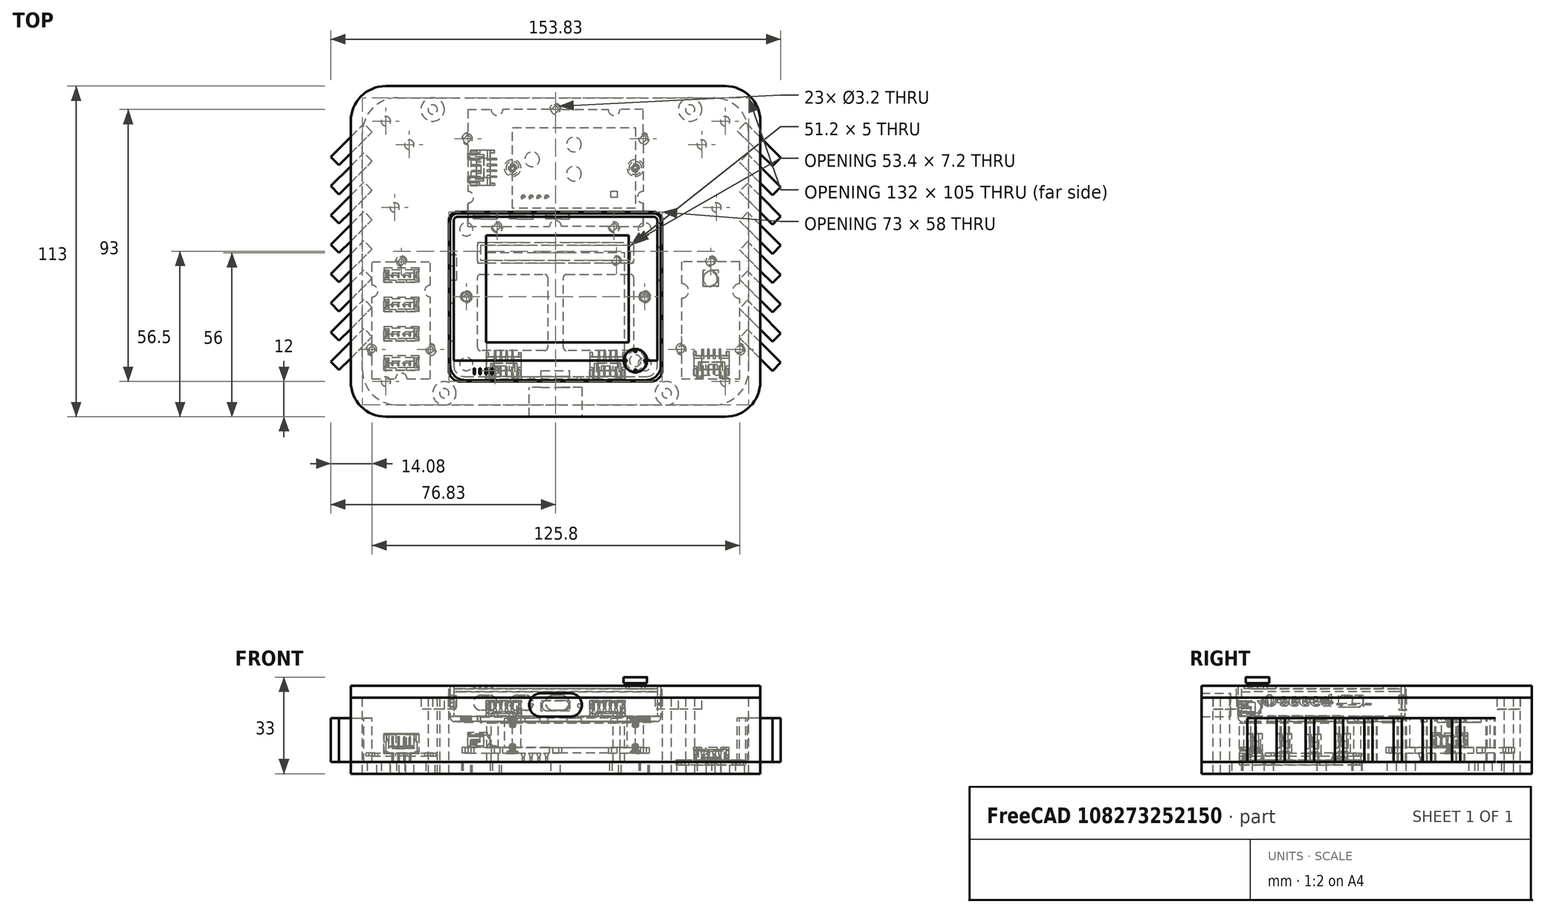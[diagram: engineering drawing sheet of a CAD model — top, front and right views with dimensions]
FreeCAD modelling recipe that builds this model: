
FCSTD DOCUMENT  (FreeCAD 0.20R29177 (Git))
Label: outBuildCopy2
License: All rights reserved
LicenseURL: http://en.wikipedia.org/wiki/All_rights_reserved
objects: Part::Cylinder×59, Part::Box×43, Part::Cut×32, Part::MultiFuse×21, Part::Feature×4, Sketcher::SketchObject×2
note: 161 computed .brp shape members not serialized (recipe doc carries the construction recipe); baked Part::Feature solids carry a one-line shape summary decoded from their .brp

FEATURE [Part::Feature] Feature  label="Grove I2C hub"
  Placement = pos=(15,60,9) rot=(0,0,1;3.14159rad)
  shape: bbox 24 x 42 x 9.849 mm, 365 faces, 5 solids (baked)
FEATURE [Part::Feature] Feature001  label="Grove_BME280"
  Placement = pos=(113,14,3) rot=(0.57735,0.57735,0.57735;2.0944rad)
  shape: bbox 23.8 x 41.9 x 6.016 mm, 221 faces, 2 solids (baked)
FEATURE [Part::Box] Box043  label="ips7100"
  AttacherType = Attacher::AttachEngine3D
  Height = 13.4
  Length = 47.1
  Width = 43.1
FEATURE [Part::Cylinder] Cylinder045  label="Cylinder"
  Angle = 360
  AttacherType = Attacher::AttachEngine3D
  FirstAngle = 0
  Height = 20
  Placement = pos=(2.75,2.75,0) rot=(0,0,1;0rad)
  Radius = 1.2
  SecondAngle = 0
FEATURE [Part::Cylinder] Cylinder046
  Angle = 360
  AttacherType = Attacher::AttachEngine3D
  FirstAngle = 0
  Height = 20
  Placement = pos=(44.35,40.35,0) rot=(0,0,1;0rad)
  Radius = 1.2
  SecondAngle = 0
FEATURE [Part::MultiFuse] Fusion030
  Shapes = -> [Cylinder045,Cylinder046]
FEATURE [Part::Cut] Cut012  label="ips7100s"
  Base = -> Box043
  Placement = pos=(46.5,13,4) rot=(0,0,1;0rad)
  Tool = -> Fusion030
FEATURE [Part::Feature] Feature002  label="Wio Terminal"
  Placement = pos=(70,41,30) rot=(0,0,1;0rad)
  shape: bbox 73.03 x 57.91 x 15.61 mm, 2405 faces, 30 solids (baked)
FEATURE [Part::Feature] Feature003  label="Seed Grove SCD30"
  Placement = pos=(40,65,9) rot=(1,0,0;4.71239rad)
  shape: bbox 64 x 44 x 15.1 mm, 422 faces, 13 solids (baked)
FEATURE [Part::Box] Box  label="base"
  AttacherType = Attacher::AttachEngine3D
  Height = 4
  Length = 140
  Width = 113
FEATURE [Part::Cylinder] Cylinder047  label="Cylinder048"
  Angle = 360
  AttacherType = Attacher::AttachEngine3D
  FirstAngle = 0
  Height = 10
  Placement = pos=(7.25,23,0) rot=(0,0,1;0rad)
  Radius = 1.6
  SecondAngle = 0
FEATURE [Part::Cylinder] Cylinder048  label="Cylinder049"
  Angle = 360
  AttacherType = Attacher::AttachEngine3D
  FirstAngle = 0
  Height = 10
  Placement = pos=(27.25,23,0) rot=(0,0,1;0rad)
  Radius = 1.6
  SecondAngle = 0
FEATURE [Part::Cylinder] Cylinder049  label="Cylinder050"
  Angle = 360
  AttacherType = Attacher::AttachEngine3D
  FirstAngle = 0
  Height = 10
  Placement = pos=(17.25,53,0) rot=(0,0,1;0rad)
  Radius = 1.6
  SecondAngle = 0
FEATURE [Part::MultiFuse] Fusion  label="i2cCuts"
  Shapes = -> [Cylinder047,Cylinder048,Cylinder049]
FEATURE [Part::Cylinder] Cylinder050  label="Cylinder051"
  Angle = 360
  AttacherType = Attacher::AttachEngine3D
  FirstAngle = 0
  Height = 10
  Placement = pos=(7.25,23,0) rot=(0,0,1;0rad)
  Radius = 1.6
  SecondAngle = 0
FEATURE [Part::Cylinder] Cylinder051  label="Cylinder052"
  Angle = 360
  AttacherType = Attacher::AttachEngine3D
  FirstAngle = 0
  Height = 10
  Placement = pos=(27.25,23,0) rot=(0,0,1;0rad)
  Radius = 1.6
  SecondAngle = 0
FEATURE [Part::Cylinder] Cylinder052  label="Cylinder053"
  Angle = 360
  AttacherType = Attacher::AttachEngine3D
  FirstAngle = 0
  Height = 10
  Placement = pos=(17.25,53,0) rot=(0,0,1;0rad)
  Radius = 1.6
  SecondAngle = 0
FEATURE [Part::MultiFuse] Fusion031  label="scdCuts001"
  Placement = pos=(105.8,0,0) rot=(0,0,1;0rad)
  Shapes = -> [Cylinder050,Cylinder051,Cylinder052]
FEATURE [Part::Cylinder] Cylinder053  label="Cylinder054"
  Angle = 360
  AttacherType = Attacher::AttachEngine3D
  FirstAngle = 0
  Height = 20
  Placement = pos=(2.75,2.75,0) rot=(0,0,1;0rad)
  Radius = 1.6
  SecondAngle = 0
FEATURE [Part::Cylinder] Cylinder054  label="Cylinder055"
  Angle = 360
  AttacherType = Attacher::AttachEngine3D
  FirstAngle = 0
  Height = 20
  Placement = pos=(44.35,40.35,0) rot=(0,0,1;0rad)
  Radius = 1.6
  SecondAngle = 0
FEATURE [Part::MultiFuse] Fusion032  label="ipsCuts"
  Placement = pos=(46.5,13,0) rot=(0,0,1;0rad)
  Shapes = -> [Cylinder053,Cylinder054]
FEATURE [Part::Cylinder] Cylinder055  label="Cylinder056"
  Angle = 360
  AttacherType = Attacher::AttachEngine3D
  FirstAngle = 0
  Height = 10
  Placement = pos=(50,65,0) rot=(0,0,1;0rad)
  Radius = 1.6
  SecondAngle = 0
FEATURE [Part::Cylinder] Cylinder056  label="Cylinder057"
  Angle = 360
  AttacherType = Attacher::AttachEngine3D
  FirstAngle = 0
  Height = 10
  Placement = pos=(90,65,0) rot=(0,0,1;0rad)
  Radius = 1.6
  SecondAngle = 0
FEATURE [Part::Cylinder] Cylinder057  label="Cylinder058"
  Angle = 360
  AttacherType = Attacher::AttachEngine3D
  FirstAngle = 0
  Height = 10
  Placement = pos=(100,95,0) rot=(0,0,1;0rad)
  Radius = 1.6
  SecondAngle = 0
FEATURE [Part::Cylinder] Cylinder058  label="Cylinder059"
  Angle = 360
  AttacherType = Attacher::AttachEngine3D
  FirstAngle = 0
  Height = 10
  Placement = pos=(40,95,0) rot=(0,0,1;0rad)
  Radius = 1.6
  SecondAngle = 0
FEATURE [Part::Cylinder] Cylinder059  label="Cylinder060"
  Angle = 360
  AttacherType = Attacher::AttachEngine3D
  FirstAngle = 0
  Height = 10
  Placement = pos=(70,105,0) rot=(0,0,1;0rad)
  Radius = 1.6
  SecondAngle = 0
FEATURE [Part::MultiFuse] Fusion033  label="scdCuts"
  Shapes = -> [Cylinder055,Cylinder056,Cylinder057,Cylinder058,Cylinder059]
FEATURE [Part::Cylinder] Cylinder060  label="Cylinder061"
  Angle = 360
  AttacherType = Attacher::AttachEngine3D
  FirstAngle = 0
  Height = 20
  Placement = pos=(39.5,41,0) rot=(0,0,1;0rad)
  Radius = 1.6
  SecondAngle = 0
FEATURE [Part::Cylinder] Cylinder061  label="Cylinder062"
  Angle = 360
  AttacherType = Attacher::AttachEngine3D
  FirstAngle = 0
  Height = 20
  Placement = pos=(100.5,41,0) rot=(0,0,1;0rad)
  Radius = 1.6
  SecondAngle = 0
FEATURE [Part::MultiFuse] Fusion034  label="wioCuts"
  Shapes = -> [Cylinder060,Cylinder061]
FEATURE [Part::MultiFuse] Fusion035  label="cuts"
  Shapes = -> [Fusion,Fusion031,Fusion032,Fusion033,Fusion034]
FEATURE [Part::Cut] Cut  label="base001"
  Base = -> Box
  Tool = -> Fusion035
FEATURE [Part::Cylinder] Cylinder062  label="Cylinder063"
  Angle = 360
  AttacherType = Attacher::AttachEngine3D
  FirstAngle = 0
  Height = 10
  Placement = pos=(12,12,0) rot=(0,0,1;0rad)
  Radius = 1.6
  SecondAngle = 0
FEATURE [Part::Cylinder] Cylinder063  label="Cylinder064"
  Angle = 360
  AttacherType = Attacher::AttachEngine3D
  FirstAngle = 0
  Height = 10
  Placement = pos=(128,12,0) rot=(0,0,1;0rad)
  Radius = 1.6
  SecondAngle = 0
FEATURE [Part::Cylinder] Cylinder064  label="Cylinder065"
  Angle = 360
  AttacherType = Attacher::AttachEngine3D
  FirstAngle = 0
  Height = 10
  Placement = pos=(12,101,0) rot=(0,0,1;0rad)
  Radius = 1.6
  SecondAngle = 0
FEATURE [Part::Cylinder] Cylinder065  label="Cylinder066"
  Angle = 360
  AttacherType = Attacher::AttachEngine3D
  FirstAngle = 0
  Height = 10
  Placement = pos=(128,101,0) rot=(0,0,1;0rad)
  Radius = 1.6
  SecondAngle = 0
FEATURE [Part::MultiFuse] Fusion036  label="outerCuts"
  Shapes = -> [Cylinder062,Cylinder063,Cylinder064,Cylinder065]
FEATURE [Part::Cut] Cut013  label="base003"
  Base = -> Cut
  Tool = -> Fusion036
FEATURE [Part::Box] Box044  label="base002"
  AttacherType = Attacher::AttachEngine3D
  Height = 4
  Length = 12
  Width = 12
FEATURE [Part::Cylinder] Cylinder  label="Cylinder067"
  Angle = 360
  AttacherType = Attacher::AttachEngine3D
  FirstAngle = 0
  Height = 10
  Placement = pos=(12,12,0) rot=(0,-0.707107,0.707107;0rad)
  Radius = 12
  SecondAngle = 0
FEATURE [Part::Cut] Cut014  label="cutOut"
  Base = -> Box044
  Tool = -> Cylinder
FEATURE [Part::Box] Box045  label="base004"
  AttacherType = Attacher::AttachEngine3D
  Height = 4
  Length = 12
  Width = 12
FEATURE [Part::Cylinder] Cylinder066  label="Cylinder068"
  Angle = 360
  AttacherType = Attacher::AttachEngine3D
  FirstAngle = 0
  Height = 10
  Placement = pos=(12,12,0) rot=(0,-0.707107,0.707107;0rad)
  Radius = 12
  SecondAngle = 0
FEATURE [Part::Cut] Cut015  label="cutOut001"
  Base = -> Box045
  Placement = pos=(140,-5.2e-15,0) rot=(0,0,1;1.5708rad)
  Tool = -> Cylinder066
FEATURE [Part::Box] Box046  label="base005"
  AttacherType = Attacher::AttachEngine3D
  Height = 4
  Length = 12
  Width = 12
FEATURE [Part::Cylinder] Cylinder067  label="Cylinder069"
  Angle = 360
  AttacherType = Attacher::AttachEngine3D
  FirstAngle = 0
  Height = 10
  Placement = pos=(12,12,0) rot=(0,-0.707107,0.707107;0rad)
  Radius = 12
  SecondAngle = 0
FEATURE [Part::Cut] Cut016  label="cutOut002"
  Base = -> Box046
  Placement = pos=(140,113,0) rot=(0,0,1;3.14159rad)
  Tool = -> Cylinder067
FEATURE [Part::Box] Box047  label="base006"
  AttacherType = Attacher::AttachEngine3D
  Height = 4
  Length = 12
  Width = 12
FEATURE [Part::Cylinder] Cylinder068  label="Cylinder070"
  Angle = 360
  AttacherType = Attacher::AttachEngine3D
  FirstAngle = 0
  Height = 10
  Placement = pos=(12,12,0) rot=(0,-0.707107,0.707107;0rad)
  Radius = 12
  SecondAngle = 0
FEATURE [Part::Cut] Cut017  label="cutOut003"
  Base = -> Box047
  Placement = pos=(0,113,0) rot=(0,0,1;4.71239rad)
  Tool = -> Cylinder068
FEATURE [Part::MultiFuse] Fusion037  label="cutOut004"
  Shapes = -> [Cut014,Cut015,Cut016,Cut017]
FEATURE [Part::Cut] Cut018
  Base = -> Cut013
  Tool = -> Fusion037
FEATURE [Part::Cylinder] Cylinder069  label="Cylinder071"
  Angle = 360
  AttacherType = Attacher::AttachEngine3D
  FirstAngle = 0
  Height = 10
  Placement = pos=(15,71.5,0) rot=(0,0,1;0rad)
  Radius = 1.6
  SecondAngle = 0
FEATURE [Part::Cylinder] Cylinder070  label="Cylinder072"
  Angle = 360
  AttacherType = Attacher::AttachEngine3D
  FirstAngle = 0
  Height = 10
  Placement = pos=(125,71.5,0) rot=(0,0,1;0rad)
  Radius = 1.6
  SecondAngle = 0
FEATURE [Part::MultiFuse] Fusion038  label="cuts001"
  Shapes = -> [Cylinder069,Cylinder070]
FEATURE [Part::Cut] Cut019  label="base007"
  Base = -> Cut018
  Tool = -> Fusion038
FEATURE [Part::Cylinder] Cylinder071  label="Cylinder073"
  Angle = 360
  AttacherType = Attacher::AttachEngine3D
  FirstAngle = 0
  Height = 10
  Placement = pos=(20,93,0) rot=(0,0,1;0rad)
  Radius = 1.6
  SecondAngle = 0
FEATURE [Part::Cylinder] Cylinder072  label="Cylinder074"
  Angle = 360
  AttacherType = Attacher::AttachEngine3D
  FirstAngle = 0
  Height = 10
  Placement = pos=(120,93,0) rot=(0,0,1;0rad)
  Radius = 1.6
  SecondAngle = 0
FEATURE [Part::MultiFuse] Fusion039  label="wallMounts"
  Shapes = -> [Cylinder071,Cylinder072]
FEATURE [Part::Cut] Cut020  label="base008"
  Base = -> Cut019
  Tool = -> Fusion039
FEATURE [Part::Box] Box048  label="top"
  AttacherType = Attacher::AttachEngine3D
  Height = 4
  Length = 140
  Width = 113
FEATURE [Part::Box] Box049  label="base009"
  AttacherType = Attacher::AttachEngine3D
  Height = 4
  Length = 12
  Width = 12
FEATURE [Part::Box] Box050  label="base010"
  AttacherType = Attacher::AttachEngine3D
  Height = 4
  Length = 12
  Width = 12
FEATURE [Part::Box] Box051  label="base011"
  AttacherType = Attacher::AttachEngine3D
  Height = 4
  Length = 12
  Width = 12
FEATURE [Part::Box] Box052  label="base012"
  AttacherType = Attacher::AttachEngine3D
  Height = 4
  Length = 12
  Width = 12
FEATURE [Part::Cylinder] Cylinder073  label="Cylinder075"
  Angle = 360
  AttacherType = Attacher::AttachEngine3D
  FirstAngle = 0
  Height = 10
  Placement = pos=(12,12,0) rot=(0,-0.707107,0.707107;0rad)
  Radius = 12
  SecondAngle = 0
FEATURE [Part::Cut] Cut021  label="cutOut005"
  Base = -> Box049
  Tool = -> Cylinder073
FEATURE [Part::Cylinder] Cylinder074  label="Cylinder076"
  Angle = 360
  AttacherType = Attacher::AttachEngine3D
  FirstAngle = 0
  Height = 10
  Placement = pos=(12,12,0) rot=(0,-0.707107,0.707107;0rad)
  Radius = 12
  SecondAngle = 0
FEATURE [Part::Cut] Cut022  label="cutOut006"
  Base = -> Box050
  Placement = pos=(140,-5.2e-15,0) rot=(0,0,1;1.5708rad)
  Tool = -> Cylinder074
FEATURE [Part::Cylinder] Cylinder075  label="Cylinder077"
  Angle = 360
  AttacherType = Attacher::AttachEngine3D
  FirstAngle = 0
  Height = 10
  Placement = pos=(12,12,0) rot=(0,-0.707107,0.707107;0rad)
  Radius = 12
  SecondAngle = 0
FEATURE [Part::Cut] Cut023  label="cutOut007"
  Base = -> Box051
  Placement = pos=(140,113,0) rot=(0,0,1;3.14159rad)
  Tool = -> Cylinder075
FEATURE [Part::Cylinder] Cylinder076  label="Cylinder078"
  Angle = 360
  AttacherType = Attacher::AttachEngine3D
  FirstAngle = 0
  Height = 10
  Placement = pos=(12,12,0) rot=(0,-0.707107,0.707107;0rad)
  Radius = 12
  SecondAngle = 0
FEATURE [Part::Cut] Cut024  label="cutOut008"
  Base = -> Box052
  Placement = pos=(0,113,0) rot=(0,0,-1;1.5708rad)
  Tool = -> Cylinder076
FEATURE [Part::MultiFuse] Fusion040  label="cutOut009"
  Shapes = -> [Cut021,Cut022,Cut023,Cut024]
FEATURE [Part::Cut] Cut025  label="top001"
  Base = -> Box048
  Placement = pos=(0,0,26) rot=(0,0,1;0rad)
  Tool = -> Fusion040
FEATURE [Part::Box] Box053  label="Cube"
  AttacherType = Attacher::AttachEngine3D
  Height = 10
  Length = 73
  Placement = pos=(33.5,12,26) rot=(0,0,1;0rad)
  Width = 58
FEATURE [Part::Box] Box054  label="Cube001"
  AttacherType = Attacher::AttachEngine3D
  Height = 10
  Length = 3
  Placement = pos=(33.5,67,26) rot=(0,0,1;0rad)
  Width = 3
FEATURE [Part::Cylinder] Cylinder077  label="Cylinder079"
  Angle = 360
  AttacherType = Attacher::AttachEngine3D
  FirstAngle = 0
  Height = 10
  Placement = pos=(36.5,67,26) rot=(0,0,1;0rad)
  Radius = 3
  SecondAngle = 0
FEATURE [Part::Cut] Cut026  label="outCutsDisplay"
  Base = -> Box054
  Tool = -> Cylinder077
FEATURE [Part::Box] Box055  label="Cube002"
  AttacherType = Attacher::AttachEngine3D
  Height = 10
  Length = 3
  Placement = pos=(33.5,67,26) rot=(0,0,1;0rad)
  Width = 3
FEATURE [Part::Cylinder] Cylinder078  label="Cylinder080"
  Angle = 360
  AttacherType = Attacher::AttachEngine3D
  FirstAngle = 0
  Height = 10
  Placement = pos=(36.5,67,26) rot=(0,0,1;0rad)
  Radius = 3
  SecondAngle = 0
FEATURE [Part::Cut] Cut027  label="outCutsDisplay001"
  Base = -> Box055
  Placement = pos=(36.5,103.5,0) rot=(0,0,1;4.71239rad)
  Tool = -> Cylinder078
FEATURE [Part::Box] Box057  label="Cube004"
  AttacherType = Attacher::AttachEngine3D
  Height = 10
  Length = 4
  Placement = pos=(32.5,67,26) rot=(0,0,1;0rad)
  Width = 4
FEATURE [Part::Cylinder] Cylinder080  label="Cylinder082"
  Angle = 360
  AttacherType = Attacher::AttachEngine3D
  FirstAngle = 0
  Height = 10
  Placement = pos=(36.5,67,26) rot=(0,0,1;0rad)
  Radius = 4
  SecondAngle = 0
FEATURE [Part::Cut] Cut029  label="outCutsDisplay003"
  Base = -> Box057
  Placement = pos=(104.5,-20.5,0) rot=(0,0,1;1.5708rad)
  Tool = -> Cylinder080
FEATURE [Part::Box] Box058  label="Cube005"
  AttacherType = Attacher::AttachEngine3D
  Height = 10
  Length = 4
  Placement = pos=(32.5,67,26) rot=(0,0,1;0rad)
  Width = 4
FEATURE [Part::Cylinder] Cylinder081  label="Cylinder083"
  Angle = 360
  AttacherType = Attacher::AttachEngine3D
  FirstAngle = 0
  Height = 10
  Placement = pos=(36.5,67,26) rot=(0,0,1;0rad)
  Radius = 4
  SecondAngle = 0
FEATURE [Part::Cut] Cut030  label="outCutsDisplay004"
  Base = -> Box058
  Placement = pos=(139,83,0) rot=(0,0,1;3.14159rad)
  Tool = -> Cylinder081
FEATURE [Part::MultiFuse] Fusion041  label="displayCuts"
  Shapes = -> [Cut029,Cut030,Cut026,Cut027]
FEATURE [Part::Cut] Cut031  label="topCut"
  Base = -> Box053
  Tool = -> Fusion041
FEATURE [Part::Cut] Cut032  label="top002"
  Base = -> Cut025
  Tool = -> Cut031
FEATURE [Part::Box] Box059  label="base013"
  AttacherType = Attacher::AttachEngine3D
  Height = 26
  Length = 140
  Width = 113
FEATURE [Part::Box] Box060  label="base014"
  AttacherType = Attacher::AttachEngine3D
  Height = 26
  Length = 12
  Width = 12
FEATURE [Part::Box] Box061  label="base015"
  AttacherType = Attacher::AttachEngine3D
  Height = 26
  Length = 12
  Width = 12
FEATURE [Part::Box] Box062  label="base016"
  AttacherType = Attacher::AttachEngine3D
  Height = 26
  Length = 12
  Width = 12
FEATURE [Part::Box] Box063  label="base017"
  AttacherType = Attacher::AttachEngine3D
  Height = 26
  Length = 12
  Width = 12
FEATURE [Part::Cylinder] Cylinder082  label="Cylinder084"
  Angle = 360
  AttacherType = Attacher::AttachEngine3D
  FirstAngle = 0
  Height = 26
  Placement = pos=(12,12,0) rot=(0,-0.707107,0.707107;0rad)
  Radius = 12
  SecondAngle = 0
FEATURE [Part::Cut] Cut033  label="cutOut010"
  Base = -> Box060
  Tool = -> Cylinder082
FEATURE [Part::Cylinder] Cylinder083  label="Cylinder085"
  Angle = 360
  AttacherType = Attacher::AttachEngine3D
  FirstAngle = 0
  Height = 26
  Placement = pos=(12,12,0) rot=(0,-0.707107,0.707107;0rad)
  Radius = 12
  SecondAngle = 0
FEATURE [Part::Cut] Cut034  label="cutOut011"
  Base = -> Box061
  Placement = pos=(140,-5.2e-15,0) rot=(0,0,1;1.5708rad)
  Tool = -> Cylinder083
FEATURE [Part::Cylinder] Cylinder084  label="Cylinder086"
  Angle = 360
  AttacherType = Attacher::AttachEngine3D
  FirstAngle = 0
  Height = 26
  Placement = pos=(12,12,0) rot=(0,-0.707107,0.707107;0rad)
  Radius = 12
  SecondAngle = 0
FEATURE [Part::Cut] Cut035  label="cutOut012"
  Base = -> Box062
  Placement = pos=(140,113,0) rot=(0,0,1;3.14159rad)
  Tool = -> Cylinder084
FEATURE [Part::Cylinder] Cylinder085  label="Cylinder087"
  Angle = 360
  AttacherType = Attacher::AttachEngine3D
  FirstAngle = 0
  Height = 26
  Placement = pos=(12,12,0) rot=(0,-0.707107,0.707107;0rad)
  Radius = 12
  SecondAngle = 0
FEATURE [Part::Cut] Cut036  label="cutOut013"
  Base = -> Box063
  Placement = pos=(0,113,0) rot=(0,0,-1;1.5708rad)
  Tool = -> Cylinder085
FEATURE [Part::MultiFuse] Fusion042  label="cuts002"
  Shapes = -> [Cut036,Cut033,Cut034,Cut035]
FEATURE [Part::Cut] Cut037  label="wall"
  Base = -> Box059
  Tool = -> Fusion042
FEATURE [Part::Box] Box064  label="base018"
  AttacherType = Attacher::AttachEngine3D
  Height = 26
  Length = 132
  Placement = pos=(4,4,0) rot=(0,0,1;0rad)
  Width = 105
FEATURE [Part::Box] Box065  label="base019"
  AttacherType = Attacher::AttachEngine3D
  Height = 26
  Length = 12
  Width = 12
FEATURE [Part::Box] Box066  label="base020"
  AttacherType = Attacher::AttachEngine3D
  Height = 26
  Length = 12
  Width = 12
FEATURE [Part::Box] Box067  label="base021"
  AttacherType = Attacher::AttachEngine3D
  Height = 26
  Length = 12
  Width = 12
FEATURE [Part::Box] Box068  label="base022"
  AttacherType = Attacher::AttachEngine3D
  Height = 26
  Length = 12
  Width = 12
FEATURE [Part::Cylinder] Cylinder086  label="Cylinder088"
  Angle = 360
  AttacherType = Attacher::AttachEngine3D
  FirstAngle = 0
  Height = 26
  Placement = pos=(12,12,0) rot=(0,-0.707107,0.707107;0rad)
  Radius = 12
  SecondAngle = 0
FEATURE [Part::Cut] Cut038  label="cutOut014"
  Base = -> Box065
  Placement = pos=(4,4,0) rot=(0,0,1;0rad)
  Tool = -> Cylinder086
FEATURE [Part::Cylinder] Cylinder087  label="Cylinder089"
  Angle = 360
  AttacherType = Attacher::AttachEngine3D
  FirstAngle = 0
  Height = 26
  Placement = pos=(12,12,0) rot=(0,-0.707107,0.707107;0rad)
  Radius = 12
  SecondAngle = 0
FEATURE [Part::Cut] Cut039  label="cutOut015"
  Base = -> Box066
  Placement = pos=(136,4,0) rot=(0,0,1;1.5708rad)
  Tool = -> Cylinder087
FEATURE [Part::Cylinder] Cylinder088  label="Cylinder090"
  Angle = 360
  AttacherType = Attacher::AttachEngine3D
  FirstAngle = 0
  Height = 26
  Placement = pos=(12,12,0) rot=(0,-0.707107,0.707107;0rad)
  Radius = 12
  SecondAngle = 0
FEATURE [Part::Cut] Cut040  label="cutOut016"
  Base = -> Box067
  Placement = pos=(136,109,0) rot=(0,0,1;3.14159rad)
  Tool = -> Cylinder088
FEATURE [Part::Cylinder] Cylinder089  label="Cylinder091"
  Angle = 360
  AttacherType = Attacher::AttachEngine3D
  FirstAngle = 0
  Height = 26
  Placement = pos=(12,12,0) rot=(0,-0.707107,0.707107;0rad)
  Radius = 12
  SecondAngle = 0
FEATURE [Part::Cut] Cut041  label="cutOut017"
  Base = -> Box068
  Placement = pos=(4,109,0) rot=(0,0,-1;1.5708rad)
  Tool = -> Cylinder089
FEATURE [Part::MultiFuse] Fusion043  label="cuts003"
  Shapes = -> [Cut041,Cut038,Cut039,Cut040]
FEATURE [Part::Cut] Cut042  label="wallCut"
  Base = -> Box064
  Tool = -> Fusion043
FEATURE [Part::Cut] Cut043  label="wall001"
  Base = -> Cut037
  Tool = -> Cut042
FEATURE [Part::Cylinder] Cylinder091  label="Cylinder093"
  Angle = 360
  AttacherType = Attacher::AttachEngine3D
  FirstAngle = 0
  Height = 4
  Placement = pos=(108,8,0) rot=(0,0,1;0rad)
  Radius = 4
  SecondAngle = 0
FEATURE [Part::Cylinder] Cylinder092  label="Cylinder094"
  Angle = 360
  AttacherType = Attacher::AttachEngine3D
  FirstAngle = 0
  Height = 4
  Placement = pos=(32,8,0) rot=(0,0,1;0rad)
  Radius = 4
  SecondAngle = 0
FEATURE [Part::Cylinder] Cylinder093  label="Cylinder095"
  Angle = 360
  AttacherType = Attacher::AttachEngine3D
  FirstAngle = 0
  Height = 4
  Placement = pos=(116,105,0) rot=(0,0,1;0rad)
  Radius = 4
  SecondAngle = 0
FEATURE [Part::Cylinder] Cylinder094  label="Cylinder096"
  Angle = 360
  AttacherType = Attacher::AttachEngine3D
  FirstAngle = 0
  Height = 4
  Placement = pos=(28,105,0) rot=(0,0,1;0rad)
  Radius = 4
  SecondAngle = 0
FEATURE [Part::MultiFuse] Fusion044  label="topMountIns"
  Placement = pos=(0,0,22) rot=(0,0,1;0rad)
  Shapes = -> [Cylinder091,Cylinder092,Cylinder093,Cylinder094]
FEATURE [Part::Cylinder] Cylinder095  label="Cylinder097"
  Angle = 360
  AttacherType = Attacher::AttachEngine3D
  FirstAngle = 0
  Height = 26
  Placement = pos=(108,8,0) rot=(0,0,1;0rad)
  Radius = 1.6
  SecondAngle = 0
FEATURE [Part::Cylinder] Cylinder096  label="Cylinder098"
  Angle = 360
  AttacherType = Attacher::AttachEngine3D
  FirstAngle = 0
  Height = 26
  Placement = pos=(32,8,0) rot=(0,0,1;0rad)
  Radius = 1.6
  SecondAngle = 0
FEATURE [Part::Cylinder] Cylinder097  label="Cylinder099"
  Angle = 360
  AttacherType = Attacher::AttachEngine3D
  FirstAngle = 0
  Height = 26
  Placement = pos=(116,105,0) rot=(0,0,1;0rad)
  Radius = 1.6
  SecondAngle = 0
FEATURE [Part::Cylinder] Cylinder098  label="Cylinder100"
  Angle = 360
  AttacherType = Attacher::AttachEngine3D
  FirstAngle = 0
  Height = 26
  Placement = pos=(28,105,0) rot=(0,0,1;0rad)
  Radius = 1.6
  SecondAngle = 0
FEATURE [Part::MultiFuse] Fusion045  label="bottomCuts"
  Shapes = -> [Cylinder095,Cylinder096,Cylinder097,Cylinder098]
FEATURE [Part::Cylinder] Cylinder099  label="Cylinder101"
  Angle = 360
  AttacherType = Attacher::AttachEngine3D
  FirstAngle = 0
  Height = 26
  Placement = pos=(108,8,0) rot=(0,0,1;0rad)
  Radius = 1.6
  SecondAngle = 0
FEATURE [Part::Cylinder] Cylinder100  label="Cylinder102"
  Angle = 360
  AttacherType = Attacher::AttachEngine3D
  FirstAngle = 0
  Height = 26
  Placement = pos=(32,8,0) rot=(0,0,1;0rad)
  Radius = 1.6
  SecondAngle = 0
FEATURE [Part::Cylinder] Cylinder101  label="Cylinder103"
  Angle = 360
  AttacherType = Attacher::AttachEngine3D
  FirstAngle = 0
  Height = 26
  Placement = pos=(116,105,0) rot=(0,0,1;0rad)
  Radius = 1.6
  SecondAngle = 0
FEATURE [Part::Cylinder] Cylinder102  label="Cylinder104"
  Angle = 360
  AttacherType = Attacher::AttachEngine3D
  FirstAngle = 0
  Height = 26
  Placement = pos=(28,105,0) rot=(0,0,1;0rad)
  Radius = 1.6
  SecondAngle = 0
FEATURE [Part::MultiFuse] Fusion046  label="topMountTop"
  Shapes = -> [Cylinder099,Cylinder100,Cylinder101,Cylinder102]
FEATURE [Part::Box] Box069  label="usbCCut"
  AttacherType = Attacher::AttachEngine3D
  Height = 8
  Length = 10
  Placement = pos=(65,0,19.5) rot=(0,0,1;0rad)
  Width = 10
FEATURE [Part::Cylinder] Cylinder103  label="usbCCut001"
  Angle = 360
  AttacherType = Attacher::AttachEngine3D
  FirstAngle = 0
  Height = 10
  Placement = pos=(65,10,23.5) rot=(1,0,0;1.5708rad)
  Radius = 4
  SecondAngle = 0
FEATURE [Part::Cylinder] Cylinder104  label="usbCCut002"
  Angle = 360
  AttacherType = Attacher::AttachEngine3D
  FirstAngle = 0
  Height = 10
  Placement = pos=(75,10,23.5) rot=(1,0,0;1.5708rad)
  Radius = 4
  SecondAngle = 0
FEATURE [Part::MultiFuse] Fusion047  label="usbCCut003"
  Shapes = -> [Box069,Cylinder103,Cylinder104]
FEATURE [Part::Box] Box070  label="ventCut"
  AttacherType = Attacher::AttachEngine3D
  Height = 15
  Length = 16
  Placement = pos=(-4,16,0) rot=(0,0,1;0.785398rad)
  Width = 4
FEATURE [Part::Box] Box071  label="ventCut001"
  AttacherType = Attacher::AttachEngine3D
  Height = 15
  Length = 16
  Placement = pos=(-4,36,0) rot=(0,0,1;0.785398rad)
  Width = 4
FEATURE [Part::Box] Box072  label="ventCut002"
  AttacherType = Attacher::AttachEngine3D
  Height = 15
  Length = 16
  Placement = pos=(-4,26,0) rot=(0,0,1;0.785398rad)
  Width = 4
FEATURE [Part::Box] Box073  label="ventCut003"
  AttacherType = Attacher::AttachEngine3D
  Height = 15
  Length = 16
  Placement = pos=(-4,46,0) rot=(0,0,1;0.785398rad)
  Width = 4
FEATURE [Part::Box] Box074  label="ventCut004"
  AttacherType = Attacher::AttachEngine3D
  Height = 15
  Length = 16
  Placement = pos=(-4,56,0) rot=(0,0,1;0.785398rad)
  Width = 4
FEATURE [Part::Box] Box075  label="ventCut005"
  AttacherType = Attacher::AttachEngine3D
  Height = 15
  Length = 16
  Placement = pos=(-4,66,0) rot=(0,0,1;0.785398rad)
  Width = 4
FEATURE [Part::Box] Box076  label="ventCut006"
  AttacherType = Attacher::AttachEngine3D
  Height = 15
  Length = 16
  Placement = pos=(-4,76,0) rot=(0,0,1;0.785398rad)
  Width = 4
FEATURE [Part::Box] Box077  label="ventCut007"
  AttacherType = Attacher::AttachEngine3D
  Height = 15
  Length = 16
  Placement = pos=(-4,86,0) rot=(0,0,1;0.785398rad)
  Width = 4
FEATURE [Part::MultiFuse] Fusion048  label="leftVents"
  Placement = pos=(0,0,4) rot=(0,0,1;0rad)
  Shapes = -> [Box070,Box071,Box072,Box073,Box074,Box075,Box076,Box077]
FEATURE [Part::Box] Box078  label="ventCut008"
  AttacherType = Attacher::AttachEngine3D
  Height = 15
  Length = 16
  Placement = pos=(-4,16,0) rot=(0,0,1;2.35619rad)
  Width = 4
FEATURE [Part::Box] Box079  label="ventCut009"
  AttacherType = Attacher::AttachEngine3D
  Height = 15
  Length = 16
  Placement = pos=(-4,36,0) rot=(0,0,1;2.35619rad)
  Width = 4
FEATURE [Part::Box] Box080  label="ventCut010"
  AttacherType = Attacher::AttachEngine3D
  Height = 15
  Length = 16
  Placement = pos=(-4,26,0) rot=(0,0,1;2.35619rad)
  Width = 4
FEATURE [Part::Box] Box081  label="ventCut011"
  AttacherType = Attacher::AttachEngine3D
  Height = 15
  Length = 16
  Placement = pos=(-4,46,0) rot=(0,0,1;2.35619rad)
  Width = 4
FEATURE [Part::Box] Box082  label="ventCut012"
  AttacherType = Attacher::AttachEngine3D
  Height = 15
  Length = 16
  Placement = pos=(-4,56,0) rot=(0,0,1;2.35619rad)
  Width = 4
FEATURE [Part::Box] Box083  label="ventCut013"
  AttacherType = Attacher::AttachEngine3D
  Height = 15
  Length = 16
  Placement = pos=(-4,66,0) rot=(0,0,1;2.35619rad)
  Width = 4
FEATURE [Part::Box] Box084  label="ventCut014"
  AttacherType = Attacher::AttachEngine3D
  Height = 15
  Length = 16
  Placement = pos=(-4,76,0) rot=(0,0,1;2.35619rad)
  Width = 4
FEATURE [Part::Box] Box085  label="ventCut015"
  AttacherType = Attacher::AttachEngine3D
  Height = 15
  Length = 17
  Placement = pos=(-4,86,0) rot=(0,0,1;2.35619rad)
  Width = 4
FEATURE [Part::MultiFuse] Fusion049  label="rightVents001"
  Placement = pos=(151,2.5,4) rot=(0,0,1;0rad)
  Shapes = -> [Box078,Box079,Box080,Box081,Box082,Box083,Box084,Box085]
FEATURE [Sketcher::SketchObject] Sketch
  FullyConstrained = true
  MapMode = 2
  Placement = pos=(-4,16,0) rot=(0,0,1;2.35619rad)
  Support = -> [Box078]
FEATURE [Sketcher::SketchObject] Sketch001
  FullyConstrained = true
